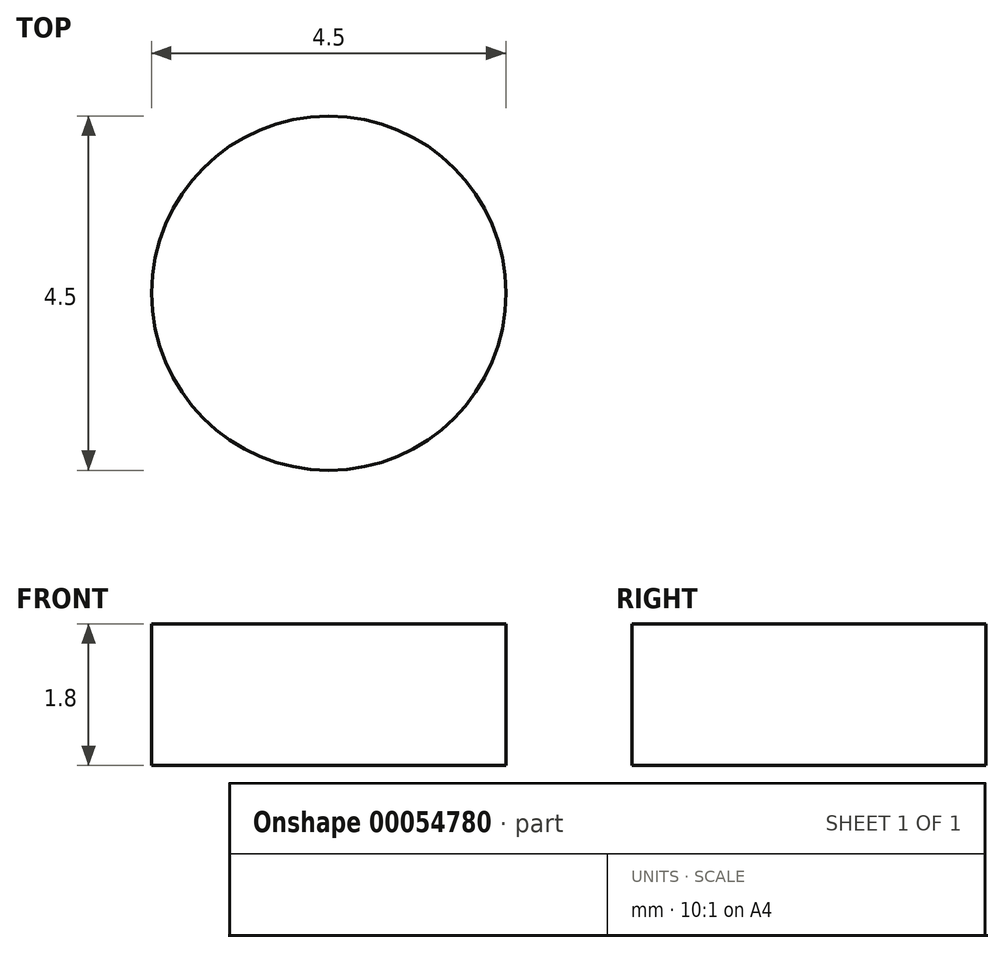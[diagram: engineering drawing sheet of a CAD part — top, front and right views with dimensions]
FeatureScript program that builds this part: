
annotation { "Feature Type Name" : "Feature", "Feature Type Description" : "" }
export const myFeature = defineFeature(function(context is Context, id is Id, definition is map)
    precondition{}
    {
        {
            var Q0;
            Q0=qCreatedBy(makeId("Top.planeOp"),FACE);
            var sketch = newSketch(context, id + "F0", { "sketchPlane" : qUnion([Q0])});
            skCircle(sketch, "E0", {"center": v(0, 0) * mm, "radius": 2.25 * mm});
            skSolve(sketch);
        }
        {
            var Q0;
            Q0=makeQuery(id+"F0.imprint","IMPRINT",FACE,{"disambiguationData":[TD([[makeQuery(id+"F0.imprint","IMPRINT",EDGE,{"derivedFrom":sQuery(id+"F0.wireOp",EDGE,"E0")}),1.0]])]});
            extrude(context, id + "F1", {"entities" : qUnion([Q0]), "depth" : 1.8 * mm});
        }
    });
